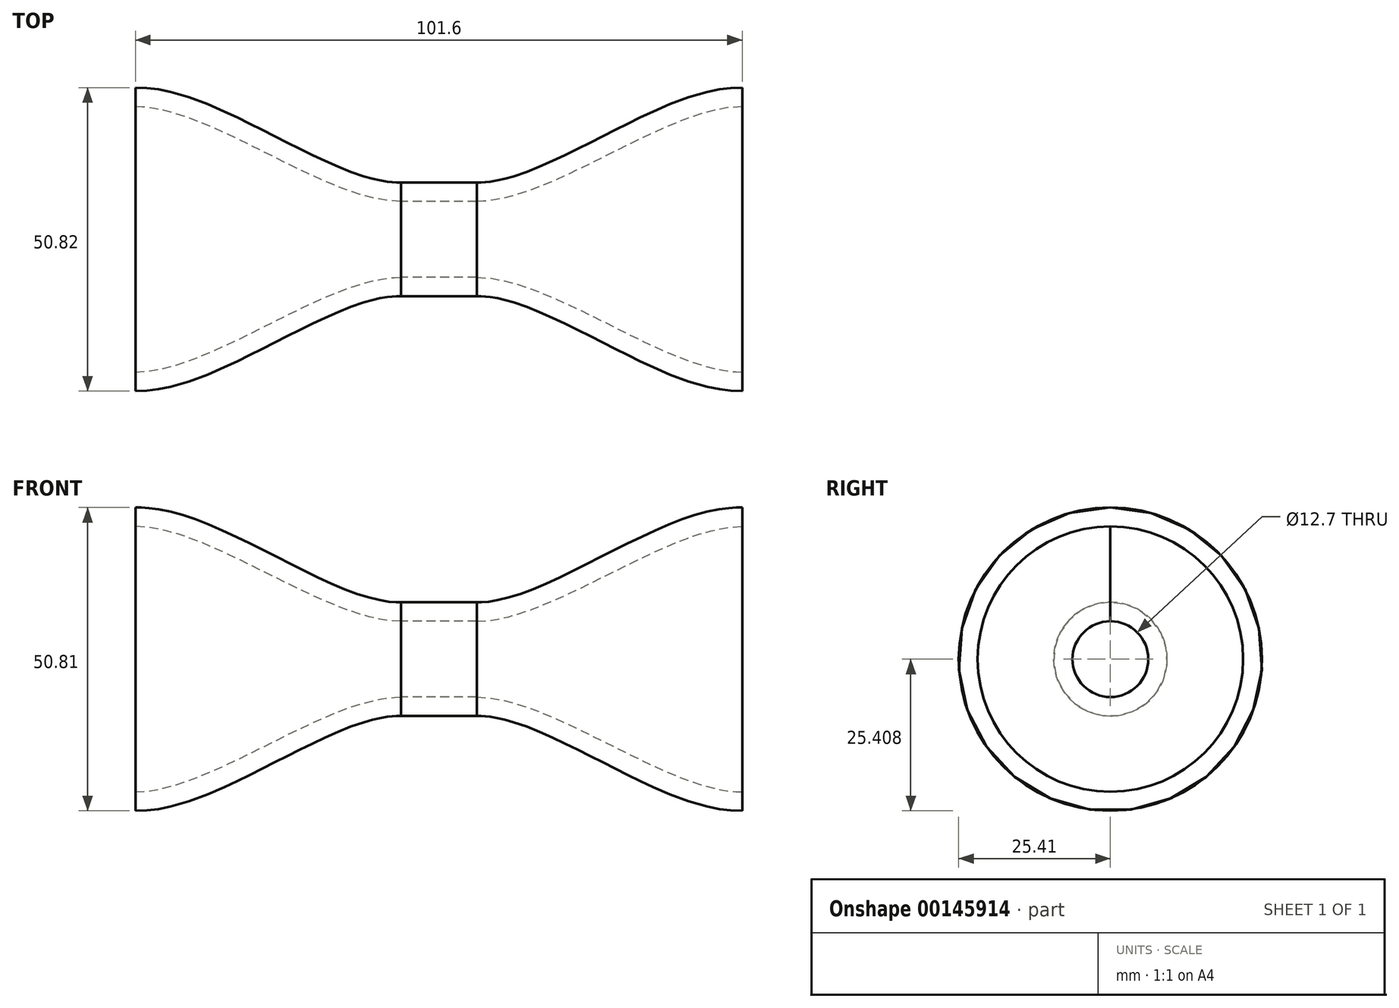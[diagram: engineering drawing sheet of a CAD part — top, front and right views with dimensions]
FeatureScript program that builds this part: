
annotation { "Feature Type Name" : "Feature", "Feature Type Description" : "" }
export const myFeature = defineFeature(function(context is Context, id is Id, definition is map)
    precondition{}
    {
        {
            var Q0;
            Q0=qCreatedBy(makeId("Front.planeOp"),FACE);
            var sketch = newSketch(context, id + "F0", { "sketchPlane" : qUnion([Q0])});
            skLineSegment(sketch, "E0", {"start": v(-66.73, 48.05) * mm, "end": v(-22.28, 48.05) * mm, "construction": true});
            skLineSegment(sketch, "E1", {"start": v(-22.28, 48.05) * mm, "end": v(-22.28, 54.4) * mm, "construction": true});
            skLineSegment(sketch, "E2", {"start": v(-66.73, 48.05) * mm, "end": v(-66.73, 70.27) * mm, "construction": true});
            skLineSegment(sketch, "E3", {"start": v(-66.73, 70.27) * mm, "end": v(-66.73, 73.45) * mm});
            skFitSpline(sketch, "E4", {"points": [v(-22.28, 54.4) * mm, v(-66.73, 70.27) * mm], "startDerivative": vector(-38.1, 0) * mm, "endDerivative": vector(-38.1, 0) * mm});
            skLineSegment(sketch, "E5", {"start": v(-34.98, 54.4) * mm, "end": v(-22.28, 54.4) * mm, "construction": true});
            skLineSegment(sketch, "E6", {"start": v(-54.03, 70.27) * mm, "end": v(-66.73, 70.27) * mm, "construction": true});
            skFitSpline(sketch, "E7.0", {"points": [v(-22.28, 57.57) * mm, v(-22.9, 57.57) * mm, v(-24.26, 57.67) * mm, v(-27.28, 58.26) * mm, v(-31.55, 59.7) * mm, v(-37.17, 62.22) * mm, v(-43.07, 65.17) * mm, v(-49.08, 68.17) * mm, v(-55.07, 70.86) * mm, v(-59.97, 72.53) * mm, v(-63.85, 73.3) * mm, v(-65.77, 73.45) * mm, v(-66.73, 73.45) * mm]});
            skLineSegment(sketch, "E8", {"start": v(-22.28, 48.05) * mm, "end": v(-15.93, 48.05) * mm, "construction": true});
            skLineSegment(sketch, "E9", {"start": v(-22.28, 54.4) * mm, "end": v(-15.93, 54.4) * mm});
            skLineSegment(sketch, "E10", {"start": v(-22.28, 57.57) * mm, "end": v(-15.93, 57.57) * mm});
            skLineSegment(sketch, "E11", {"start": v(-15.93, 48.05) * mm, "end": v(-15.93, 54.4) * mm, "construction": true});
            skLineSegment(sketch, "E12.MirrorCS", {"start": v(-9.58, 57.57) * mm, "end": v(-15.93, 57.57) * mm});
            skLineSegment(sketch, "E13.MirrorCS", {"start": v(-9.58, 54.4) * mm, "end": v(-15.93, 54.4) * mm});
            skFitSpline(sketch, "E14.MirrorCS", {"points": [v(-9.58, 54.4) * mm, v(34.87, 70.27) * mm], "startDerivative": vector(38.1, 0) * mm, "endDerivative": vector(38.1, 0) * mm});
            skLineSegment(sketch, "E15.MirrorCS", {"start": v(34.87, 70.27) * mm, "end": v(34.87, 73.45) * mm});
            skFitSpline(sketch, "E16.0", {"points": [v(-9.58, 57.57) * mm, v(-8.95, 57.57) * mm, v(-7.6, 57.67) * mm, v(-4.58, 58.26) * mm, v(-0.31, 59.7) * mm, v(5.3, 62.22) * mm, v(11.2, 65.17) * mm, v(17.21, 68.17) * mm, v(23.2, 70.86) * mm, v(28.1, 72.53) * mm, v(31.98, 73.3) * mm, v(33.9, 73.45) * mm, v(34.87, 73.45) * mm]});
            skSolve(sketch);
        }
        {
            var Q0;
            Q0=makeQuery(id+"F0.imprint","IMPRINT",FACE,{"disambiguationData":[TD([[makeQuery(id+"F0.imprint","IMPRINT",EDGE,{"derivedFrom":sQuery(id+"F0.wireOp",EDGE,"E3")}),-1.0]])]});
            var Q1;
            Q1=sQuery(id+"F0.wireOp",EDGE,"E0");
            revolve(context, id + "F1", {"entities" : qUnion([Q0]), "axis" : qUnion([Q1]), "revolveType" : RevolveType.FULL});
        }
    });
